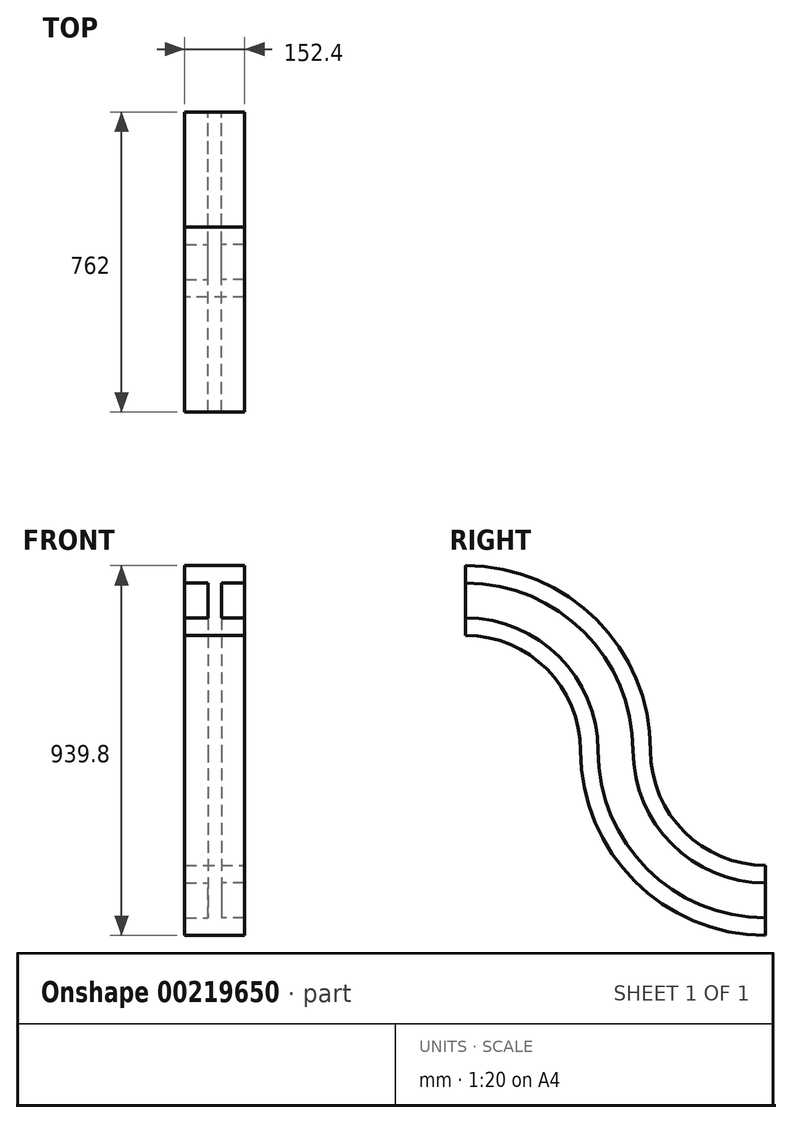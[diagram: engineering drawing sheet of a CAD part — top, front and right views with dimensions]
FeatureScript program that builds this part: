
annotation { "Feature Type Name" : "Feature", "Feature Type Description" : "" }
export const myFeature = defineFeature(function(context is Context, id is Id, definition is map)
    precondition{}
    {
        {
            var Q0;
            Q0=qCreatedBy(makeId("Front.planeOp"),FACE);
            var sketch = newSketch(context, id + "F0", { "sketchPlane" : qUnion([Q0])});
            skLineSegment(sketch, "E0", {"start": v(0, 88.9) * mm, "end": v(76.2, 88.9) * mm});
            skLineSegment(sketch, "E1", {"start": v(76.2, 88.9) * mm, "end": v(76.2, 44.45) * mm});
            skLineSegment(sketch, "E2", {"start": v(76.2, 44.45) * mm, "end": v(17.37, 44.45) * mm});
            skLineSegment(sketch, "E3", {"start": v(0, 88.9) * mm, "end": v(0, -88.9) * mm, "construction": true});
            skLineSegment(sketch, "E4", {"start": v(-17.37, 0) * mm, "end": v(17.37, 0) * mm, "construction": true});
            skLineSegment(sketch, "E5", {"start": v(17.37, 0) * mm, "end": v(17.37, 44.45) * mm});
            skLineSegment(sketch, "E6.MirrorCS", {"start": v(0, 88.9) * mm, "end": v(-76.2, 88.9) * mm});
            skLineSegment(sketch, "E7.MirrorCS", {"start": v(-76.2, 88.9) * mm, "end": v(-76.2, 44.45) * mm});
            skLineSegment(sketch, "E8.MirrorCS", {"start": v(-17.37, 0) * mm, "end": v(-17.37, 44.45) * mm});
            skLineSegment(sketch, "E9.MirrorCS", {"start": v(-76.2, 44.45) * mm, "end": v(-17.37, 44.45) * mm});
            skLineSegment(sketch, "E10.MirrorCS", {"start": v(0, -88.9) * mm, "end": v(-76.2, -88.9) * mm});
            skLineSegment(sketch, "E11.MirrorCS", {"start": v(-76.2, -88.9) * mm, "end": v(-76.2, -44.45) * mm});
            skLineSegment(sketch, "E12.MirrorCS", {"start": v(-76.2, -44.45) * mm, "end": v(-17.37, -44.45) * mm});
            skLineSegment(sketch, "E13.MirrorCS", {"start": v(-17.37, 0) * mm, "end": v(-17.37, -44.45) * mm});
            skLineSegment(sketch, "E14.MirrorCS", {"start": v(76.2, -44.45) * mm, "end": v(17.37, -44.45) * mm});
            skLineSegment(sketch, "E15.MirrorCS", {"start": v(0, -88.9) * mm, "end": v(76.2, -88.9) * mm});
            skLineSegment(sketch, "E16.MirrorCS", {"start": v(17.37, 0) * mm, "end": v(17.37, -44.45) * mm});
            skLineSegment(sketch, "E17.MirrorCS", {"start": v(76.2, -88.9) * mm, "end": v(76.2, -44.45) * mm});
            skSolve(sketch);
        }
        {
            var Q0;
            Q0=qCreatedBy(makeId("Right.planeOp"),FACE);
            var sketch = newSketch(context, id + "F1", { "sketchPlane" : qUnion([Q0])});
            skArc(sketch, "E18", {"start": v(0, 0) * mm, "mid": v(269.4, -111.6) * mm, "end": v(381, -381) * mm});
            skArc(sketch, "E19", {"start": v(381, -381) * mm, "mid": v(492.6, -650.4) * mm, "end": v(762, -762) * mm});
            skSolve(sketch);
        }
        {
            var Q0;
            Q0=makeQuery(id+"F0.imprint","IMPRINT",FACE,{"disambiguationData":[TD([[makeQuery(id+"F0.imprint","IMPRINT",EDGE,{"derivedFrom":sQuery(id+"F0.wireOp",EDGE,"E0")}),-1.0]])]});
            var Q1;
            Q1=sQuery(id+"F1.wireOp",EDGE,"E19");
            var Q2;
            Q2=sQuery(id+"F1.wireOp",EDGE,"E18");
            sweep(context, id + "F2", {"profiles" : qUnion([Q0]), "path" : qUnion([Q1, Q2])});
        }
        {
            var Q0;
            Q0=makeQuery(id+"F0.imprint","IMPRINT",FACE,{"disambiguationData":[TD([[makeQuery(id+"F0.imprint","IMPRINT",EDGE,{"derivedFrom":sQuery(id+"F0.wireOp",EDGE,"E0")}),-1.0]])]});
            var Q1;
            Q1=sQuery(id+"F1.wireOp",EDGE,"E18");
            var Q2;
            Q2=sQuery(id+"F1.wireOp",EDGE,"E19");
            sweep(context, id + "F3", {"profiles" : qUnion([Q0]), "path" : qUnion([Q1, Q2])});
        }
    });
